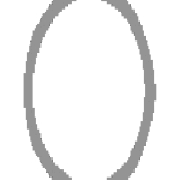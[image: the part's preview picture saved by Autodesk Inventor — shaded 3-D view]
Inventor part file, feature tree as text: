
AUTODESK INVENTOR PART (.ipt)
format: ipt  version: 2021 (Build 250183000, 183)  size: 114,176 bytes
history: native  units: in
note: dims shown in document units (in); Inventor stores cm internally (conversion verified against a paired STEP export)
features: other x4, sketch x3, plane x1
ambient origin geometry x8: Origin, YZ Plane, XZ Plane, XY Plane, X Axis, Y Axis, Z Axis, Center Point
bodies: Solid1 (feature_tree), Body (feature_tree)
feature tree (8):
  other  "Driven Length"
  other  "Frame Generator"
  other  "Start Plane"
  other  "End Plane"
  sketch  "Sketch"  dims[d2=6.0828in d4=-0.0in d5=6.0828in d6=0.12in d7=0.0in d8=90.0deg d9=6.0828in]
  sketch  "Sketch2"  dims[d0=1.0in]
  plane  "Work Plane3"
  sketch  "Sketch3"  dims[d1=0.065in]
